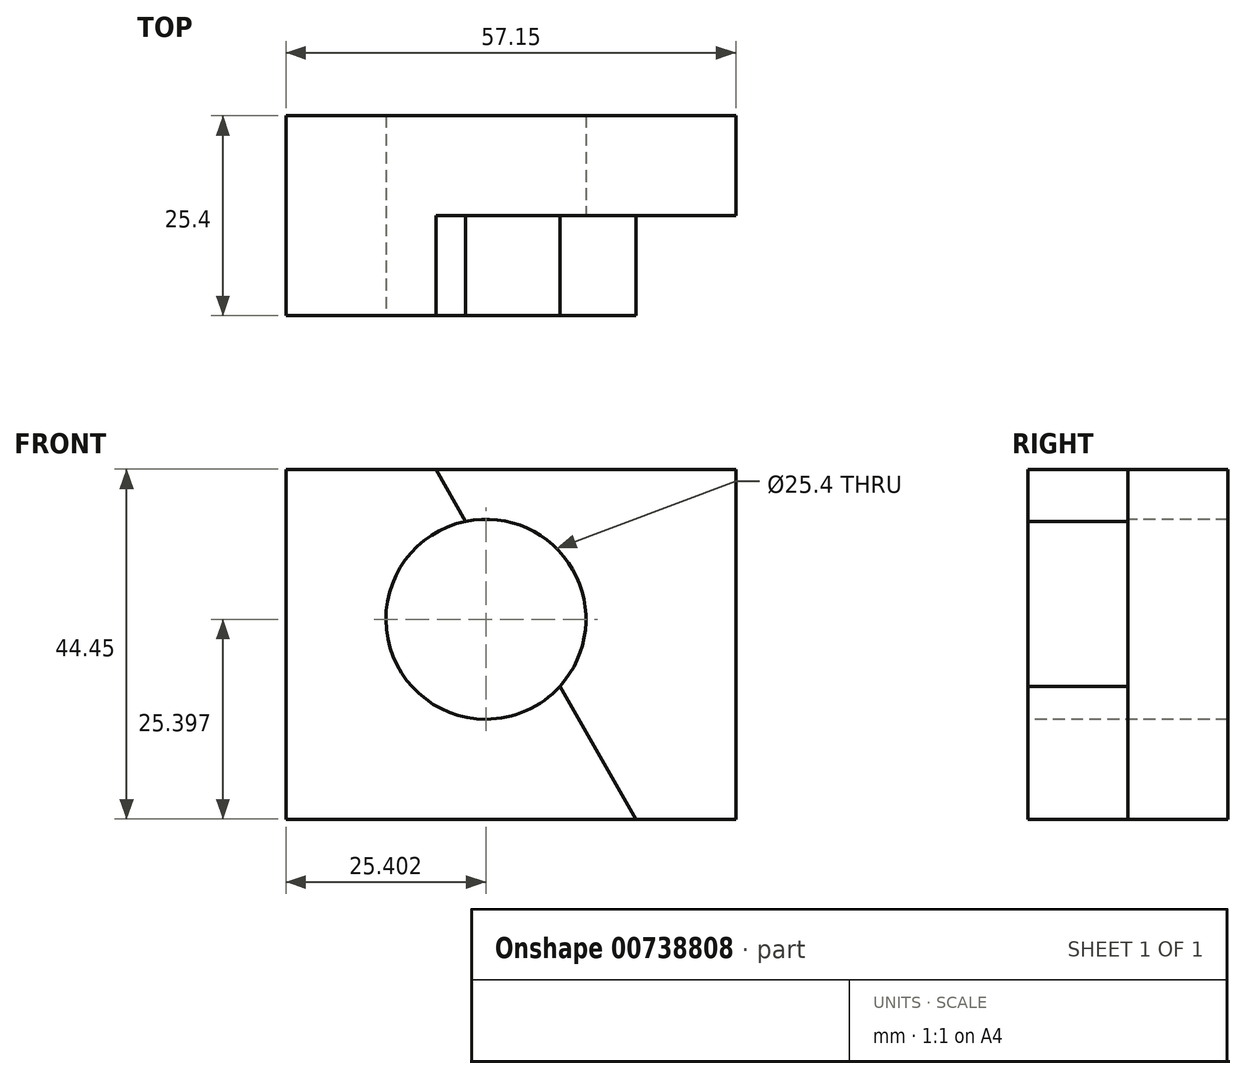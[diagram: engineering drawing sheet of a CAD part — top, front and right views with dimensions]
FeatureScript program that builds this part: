
annotation { "Feature Type Name" : "Feature", "Feature Type Description" : "" }
export const myFeature = defineFeature(function(context is Context, id is Id, definition is map)
    precondition{}
    {
        {
            var Q0;
            Q0=qCreatedBy(makeId("Front.planeOp"),FACE);
            var sketch = newSketch(context, id + "F0", { "sketchPlane" : qUnion([Q0])});
            skLineSegment(sketch, "E0.bottom", {"start": v(-27.17, 31.4) * mm, "end": v(29.98, 31.4) * mm});
            skLineSegment(sketch, "E0.top", {"start": v(-27.17, -13.05) * mm, "end": v(29.98, -13.05) * mm});
            skLineSegment(sketch, "E0.left", {"start": v(-27.17, 31.4) * mm, "end": v(-27.17, -13.05) * mm});
            skLineSegment(sketch, "E0.right", {"start": v(29.98, 31.4) * mm, "end": v(29.98, -13.05) * mm});
            skSolve(sketch);
        }
        {
            var Q0;
            Q0 = qSketchRegion(id + "F0", true);
            extrude(context, id + "F1", {"entities" : qUnion([Q0]), "depth" : 25.4 * mm, "offsetDistance" : 25.4 * mm});
        }
        {
            var Q0;
            Q0=makeQuery(id+"F1.opExtrude","CAP_FACE",FACE,{"disambiguationData":[OSD([sQuery(id+"F0.wireOp",EDGE,"E0.bottom"),sQuery(id+"F0.wireOp",EDGE,"E0.top"),sQuery(id+"F0.wireOp",EDGE,"E0.left"),sQuery(id+"F0.wireOp",EDGE,"E0.right")])],"isStart":false});
            var sketch = newSketch(context, id + "F2", { "sketchPlane" : qUnion([Q0])});
            skLineSegment(sketch, "E1", {"start": v(-14.47, 31.4) * mm, "end": v(-14.47, -13.05) * mm});
            skLineSegment(sketch, "E2", {"start": v(-27.17, -0.35) * mm, "end": v(29.98, -0.35) * mm});
            skLineSegment(sketch, "E3", {"start": v(10.93, 31.4) * mm, "end": v(10.93, -13.05) * mm});
            skLineSegment(sketch, "E4", {"start": v(-27.17, 25.05) * mm, "end": v(29.98, 25.05) * mm});
            skCircle(sketch, "E5", {"center": v(-1.77, 12.35) * mm, "radius": 12.7 * mm});
            skSolve(sketch);
        }
        {
            var Q0;
            {var subQ0=sQuery(id+"F2.wireOp",EDGE,"E5");var subQ1=makeQuery(id+"F2.imprint","INTERSECT",VERTEX,{"derivedFrom":[sQuery(id+"F2.wireOp",EDGE,"E3"),subQ0]});Q0=makeQuery(id+"F2.imprint","IMPRINT",FACE,{"disambiguationData":[TD([[makeQuery(id+"F2.imprint","IMPRINT",EDGE,{"disambiguationData":[TD([[subQ1,-1.0]])],"derivedFrom":subQ0}),1.0]])]});}
            extrude(context, id + "F3", {"entities" : qUnion([Q0]), "operationType" : NewBodyOperationType.REMOVE, "endBound" : BoundingType.THROUGH_ALL, "oppositeDirection" : true, "depth" : 25.4 * mm, "offsetDistance" : 25.4 * mm});
        }
        {
            var Q0;
            Q0=makeQuery(id+"F1.opExtrude","CAP_FACE",FACE,{"disambiguationData":[OSD([sQuery(id+"F0.wireOp",EDGE,"E0.bottom"),sQuery(id+"F0.wireOp",EDGE,"E0.top"),sQuery(id+"F0.wireOp",EDGE,"E0.left"),sQuery(id+"F0.wireOp",EDGE,"E0.right")])],"isStart":false});
            var sketch = newSketch(context, id + "F4", { "sketchPlane" : qUnion([Q0])});
            skLineSegment(sketch, "E6", {"start": v(-8.12, 31.4) * mm, "end": v(17.28, -13.05) * mm});
            skSolve(sketch);
        }
        {
            var Q0;
            Q0 = qSketchRegion(id + "F4", true);
            var Q1;
            {var subQ0=makeQuery(id+"F1.opExtrude","CAP_EDGE",EDGE,{"disambiguationData":[OSD([sQuery(id+"F0.wireOp",EDGE,"E0.right")])],"isStart":false});Q1=makeQuery(id+"F4.imprint","IMPRINT",FACE,{"disambiguationData":[TD([[makeQuery(id+"F4.imprint","IMPRINT",EDGE,{"derivedFrom":subQ0}),-1.0]])]});}
            extrude(context, id + "F5", {"entities" : qUnion([Q0, Q1]), "operationType" : NewBodyOperationType.REMOVE, "oppositeDirection" : true, "depth" : 12.7 * mm, "offsetDistance" : 25.4 * mm});
        }
    });
